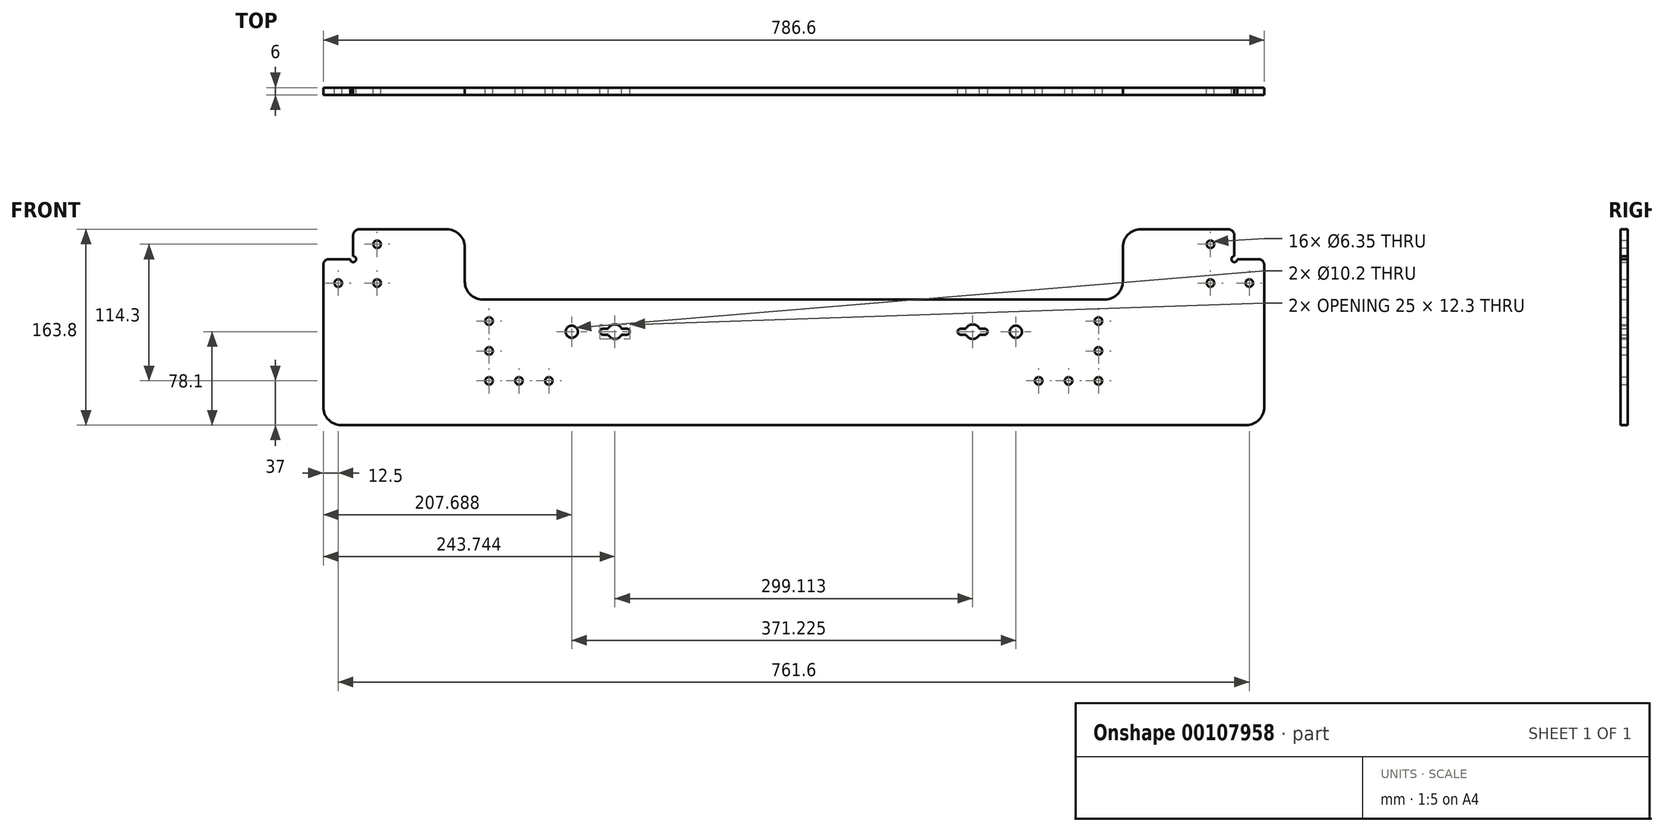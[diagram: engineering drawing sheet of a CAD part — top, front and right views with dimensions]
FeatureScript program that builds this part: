
annotation { "Feature Type Name" : "Feature", "Feature Type Description" : "" }
export const myFeature = defineFeature(function(context is Context, id is Id, definition is map)
    precondition{}
    {
        {
            var Q0;
            Q0=qCreatedBy(makeId("Front.planeOp"),FACE);
            var sketch = newSketch(context, id + "F0", { "sketchPlane" : qUnion([Q0])});
            skLineSegment(sketch, "E0", {"start": v(0, 0) * mm, "end": v(239.71, 0) * mm, "construction": true});
            skLineSegment(sketch, "E1", {"start": v(239.71, 0) * mm, "end": v(239.71, -48) * mm, "construction": true});
            skCircle(sketch, "E2", {"center": v(185.61, -26.9) * mm, "radius": 5.1 * mm});
            skLineSegment(sketch, "E3", {"start": v(0, 0) * mm, "end": v(0, 0) * mm});
            skLineSegment(sketch, "E4", {"start": v(239.71, 0) * mm, "end": v(239.71, 0) * mm});
            skLineSegment(sketch, "E5", {"start": v(239.71, -48) * mm, "end": v(0, -48) * mm, "construction": true});
            skLineSegment(sketch, "E6", {"start": v(0, -48) * mm, "end": v(0, 0) * mm, "construction": true});
            skLineSegment(sketch, "E7", {"start": v(368.3, 53.8) * mm, "end": v(368.3, 33.8) * mm});
            skLineSegment(sketch, "E8", {"start": v(368.3, 33.8) * mm, "end": v(388.3, 33.8) * mm});
            skLineSegment(sketch, "E9", {"start": v(393.3, 28.8) * mm, "end": v(393.3, -90) * mm});
            skLineSegment(sketch, "E10", {"start": v(378.3, -105) * mm, "end": v(0, -105) * mm});
            skLineSegment(sketch, "E11", {"start": v(393.3, 33.8) * mm, "end": v(393.3, 58.8) * mm, "construction": true});
            skLineSegment(sketch, "E12", {"start": v(393.3, 58.8) * mm, "end": v(368.3, 58.8) * mm, "construction": true});
            skLineSegment(sketch, "E13", {"start": v(368.3, 33.8) * mm, "end": v(393.3, 58.8) * mm, "construction": true});
            skLineSegment(sketch, "E14", {"start": v(393.3, 33.8) * mm, "end": v(368.3, 58.8) * mm, "construction": true});
            skLineSegment(sketch, "E15", {"start": v(0, 0) * mm, "end": v(0, -93) * mm, "construction": true});
            skLineSegment(sketch, "E16", {"start": v(0, -93) * mm, "end": v(70, -93) * mm, "construction": true});
            skCircle(sketch, "E17", {"center": v(149.56, -26.9) * mm, "radius": 6.15 * mm});
            skCircle(sketch, "E18", {"center": v(159.56, -26.88) * mm, "radius": 2.5 * mm});
            skLineSegment(sketch, "E19", {"start": v(159.56, -24.38) * mm, "end": v(149.56, -24.38) * mm});
            skLineSegment(sketch, "E20.MirrorCS", {"start": v(159.56, -29.38) * mm, "end": v(149.56, -29.38) * mm});
            skLineSegment(sketch, "E21.MirrorCS", {"start": v(139.56, -24.38) * mm, "end": v(149.56, -24.38) * mm});
            skLineSegment(sketch, "E22.MirrorCS", {"start": v(139.56, -29.38) * mm, "end": v(149.56, -29.38) * mm});
            skCircle(sketch, "E23.MirrorC", {"center": v(139.56, -26.88) * mm, "radius": 2.5 * mm});
            skLineSegment(sketch, "E24.MirrorCS", {"start": v(-368.3, 53.8) * mm, "end": v(-368.3, 33.8) * mm});
            skLineSegment(sketch, "E25.MirrorCS", {"start": v(-368.3, 33.8) * mm, "end": v(-388.3, 33.8) * mm});
            skLineSegment(sketch, "E26.MirrorCS", {"start": v(-393.3, 28.8) * mm, "end": v(-393.3, -90) * mm});
            skLineSegment(sketch, "E27.MirrorCS", {"start": v(-378.3, -105) * mm, "end": v(0, -105) * mm});
            skCircle(sketch, "E28.MirrorC", {"center": v(-149.56, -26.9) * mm, "radius": 6.15 * mm});
            skLineSegment(sketch, "E29.MirrorCS", {"start": v(-139.56, -29.38) * mm, "end": v(-149.56, -29.38) * mm});
            skCircle(sketch, "E30.MirrorC", {"center": v(-185.61, -26.9) * mm, "radius": 5.1 * mm});
            skCircle(sketch, "E31.MirrorC", {"center": v(-159.56, -26.88) * mm, "radius": 2.5 * mm});
            skLineSegment(sketch, "E32.MirrorCS", {"start": v(-159.56, -29.38) * mm, "end": v(-149.56, -29.38) * mm});
            skLineSegment(sketch, "E33.MirrorCS", {"start": v(-159.56, -24.38) * mm, "end": v(-149.56, -24.38) * mm});
            skLineSegment(sketch, "E34.MirrorCS", {"start": v(-139.56, -24.38) * mm, "end": v(-149.56, -24.38) * mm});
            skCircle(sketch, "E35.MirrorC", {"center": v(-139.56, -26.88) * mm, "radius": 2.5 * mm});
            skCircle(sketch, "E36", {"center": v(-368.3, 33.8) * mm, "radius": 2.5 * mm});
            skCircle(sketch, "E37", {"center": v(368.3, 33.8) * mm, "radius": 2.5 * mm});
            skCircle(sketch, "E38", {"center": v(254.71, -68) * mm, "radius": 3.18 * mm});
            skCircle(sketch, "E39.0.1.0", {"center": v(254.71, -43) * mm, "radius": 3.18 * mm});
            skCircle(sketch, "E39.0.2.0", {"center": v(254.71, -18) * mm, "radius": 3.18 * mm});
            skLineSegment(sketch, "E39.direction1", {"start": v(254.71, -68) * mm, "end": v(229.71, -68) * mm, "construction": true});
            skLineSegment(sketch, "E39.direction2", {"start": v(254.71, -68) * mm, "end": v(254.71, -43) * mm, "construction": true});
            skCircle(sketch, "E40.1.0.0", {"center": v(229.71, -68) * mm, "radius": 3.18 * mm});
            skCircle(sketch, "E40.2.0.0", {"center": v(204.71, -68) * mm, "radius": 3.18 * mm});
            skCircle(sketch, "E41", {"center": v(348.3, 13.8) * mm, "radius": 3.18 * mm});
            skLineSegment(sketch, "E42", {"start": v(368.3, 46.3) * mm, "end": v(326.4, 46.3) * mm, "construction": true});
            skLineSegment(sketch, "E43", {"start": v(380.8, 33.8) * mm, "end": v(380.8, -6.04) * mm, "construction": true});
            skLineSegment(sketch, "E44", {"start": v(348.3, 13.8) * mm, "end": v(380.8, 13.8) * mm, "construction": true});
            skLineSegment(sketch, "E45", {"start": v(348.3, 13.8) * mm, "end": v(348.3, 46.3) * mm, "construction": true});
            skCircle(sketch, "E46", {"center": v(348.3, 46.3) * mm, "radius": 3.18 * mm});
            skCircle(sketch, "E47", {"center": v(380.8, 13.8) * mm, "radius": 3.18 * mm});
            skLineSegment(sketch, "E48", {"start": v(363.3, 58.8) * mm, "end": v(290, 58.8) * mm});
            skLineSegment(sketch, "E49", {"start": v(275, 43.8) * mm, "end": v(275, 15) * mm});
            skLineSegment(sketch, "E50", {"start": v(260, 0) * mm, "end": v(0, 0) * mm});
            skCircle(sketch, "E51.MirrorC", {"center": v(-254.71, -18) * mm, "radius": 3.18 * mm});
            skCircle(sketch, "E52.MirrorC", {"center": v(-254.71, -43) * mm, "radius": 3.18 * mm});
            skCircle(sketch, "E53.MirrorC", {"center": v(-254.71, -68) * mm, "radius": 3.18 * mm});
            skCircle(sketch, "E54.MirrorC", {"center": v(-229.71, -68) * mm, "radius": 3.18 * mm});
            skCircle(sketch, "E55.MirrorC", {"center": v(-204.71, -68) * mm, "radius": 3.18 * mm});
            skLineSegment(sketch, "E56.MirrorCS", {"start": v(-260, 0) * mm, "end": v(0, 0) * mm});
            skLineSegment(sketch, "E57.MirrorCS", {"start": v(-275, 43.8) * mm, "end": v(-275, 15) * mm});
            skLineSegment(sketch, "E58.MirrorCS", {"start": v(-363.3, 58.8) * mm, "end": v(-290, 58.8) * mm});
            skCircle(sketch, "E59.MirrorC", {"center": v(-348.3, 46.3) * mm, "radius": 3.18 * mm});
            skCircle(sketch, "E60.MirrorC", {"center": v(-348.3, 13.8) * mm, "radius": 3.18 * mm});
            skCircle(sketch, "E61.MirrorC", {"center": v(-380.8, 13.8) * mm, "radius": 3.18 * mm});
            skPoint(sketch, "E62.visualSharp", {"position": v(-275, 58.8) * mm});
            skArc(sketch, "E62.filletArc", {"start": v(-275, 43.8) * mm, "mid": v(-279.4, 54.4) * mm, "end": v(-290, 58.8) * mm});
            skPoint(sketch, "E63.visualSharp", {"position": v(-275, 0) * mm});
            skArc(sketch, "E63.filletArc", {"start": v(-275, 15) * mm, "mid": v(-270.6, 4.4) * mm, "end": v(-260, 0) * mm});
            skPoint(sketch, "E64.visualSharp", {"position": v(-393.3, -105) * mm});
            skArc(sketch, "E64.filletArc", {"start": v(-393.3, -90) * mm, "mid": v(-388.9, -100.6) * mm, "end": v(-378.3, -105) * mm});
            skPoint(sketch, "E65.visualSharp", {"position": v(275, 0) * mm});
            skArc(sketch, "E65.filletArc", {"start": v(260, 0) * mm, "mid": v(270.6, 4.4) * mm, "end": v(275, 15) * mm});
            skPoint(sketch, "E66.visualSharp", {"position": v(275, 58.8) * mm});
            skArc(sketch, "E66.filletArc", {"start": v(290, 58.8) * mm, "mid": v(279.4, 54.4) * mm, "end": v(275, 43.8) * mm});
            skPoint(sketch, "E67.visualSharp", {"position": v(393.3, -105) * mm});
            skArc(sketch, "E67.filletArc", {"start": v(378.3, -105) * mm, "mid": v(388.9, -100.6) * mm, "end": v(393.3, -90) * mm});
            skPoint(sketch, "E68.visualSharp", {"position": v(393.3, 33.8) * mm});
            skArc(sketch, "E68.filletArc", {"start": v(393.3, 28.8) * mm, "mid": v(391.84, 32.34) * mm, "end": v(388.3, 33.8) * mm});
            skPoint(sketch, "E69.visualSharp", {"position": v(-368.3, 58.8) * mm});
            skArc(sketch, "E69.filletArc", {"start": v(-363.3, 58.8) * mm, "mid": v(-366.84, 57.34) * mm, "end": v(-368.3, 53.8) * mm});
            skPoint(sketch, "E70.visualSharp", {"position": v(-393.3, 33.8) * mm});
            skArc(sketch, "E70.filletArc", {"start": v(-388.3, 33.8) * mm, "mid": v(-391.84, 32.34) * mm, "end": v(-393.3, 28.8) * mm});
            skPoint(sketch, "E71.visualSharp", {"position": v(368.3, 58.8) * mm});
            skArc(sketch, "E71.filletArc", {"start": v(368.3, 53.8) * mm, "mid": v(366.84, 57.34) * mm, "end": v(363.3, 58.8) * mm});
            skSolve(sketch);
        }
        {
            var Q0;
            Q0=makeQuery(id+"F0.imprint","IMPRINT",FACE,{"disambiguationData":[TD([[makeQuery(id+"F0.imprint","IMPRINT",EDGE,{"derivedFrom":sQuery(id+"F0.wireOp",EDGE,"E2")}),-1.0]])]});
            extrude(context, id + "F1", {"entities" : qUnion([Q0]), "depth" : 6 * mm});
        }
    });
